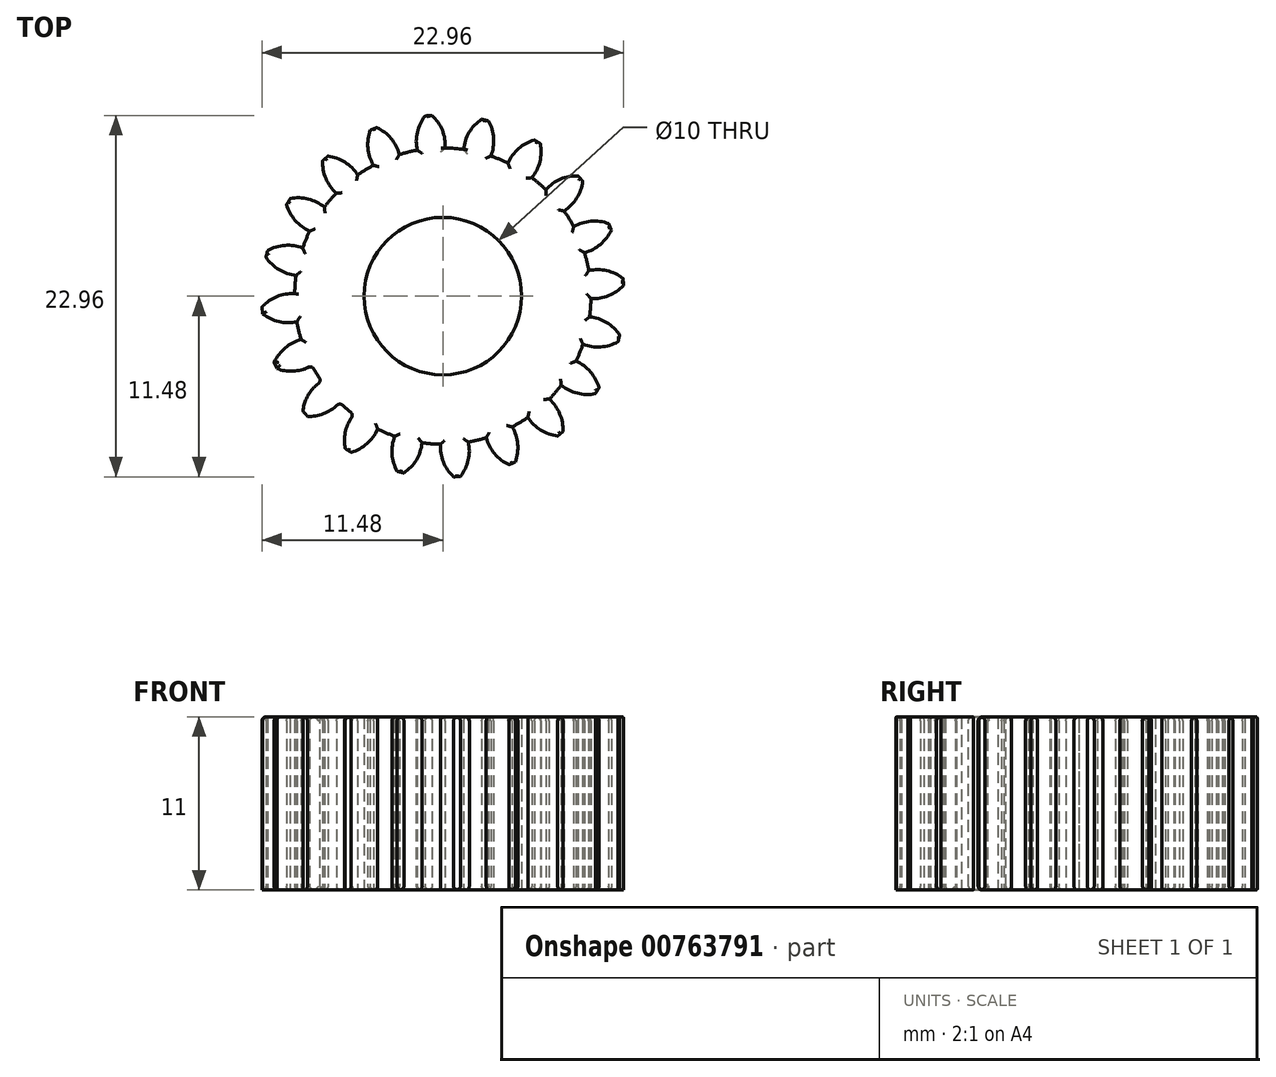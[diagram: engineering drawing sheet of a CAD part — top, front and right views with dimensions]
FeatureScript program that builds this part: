
annotation { "Feature Type Name" : "Feature", "Feature Type Description" : "" }
export const myFeature = defineFeature(function(context is Context, id is Id, definition is map)
    precondition{}
    {
        {
            assignVariable(context, id + "F0", {"name" : "GearDepth", "anyValue" : 1});
        }
        {
            assignVariable(context, id + "F1", {"name" : "TeethFillet", "anyValue" : getVariable(context, 'GearDepth') * .25});
        }
        {
            var Q0;
            Q0=qCreatedBy(makeId("Top.planeOp"),FACE);
            var sketch = newSketch(context, id + "F2", { "sketchPlane" : qUnion([Q0])});
            skCircle(sketch, "E0", {"center": v(0, 0) * mm, "radius": 9.4 * mm});
            skCircle(sketch, "E1", {"center": v(0, 0) * mm, "radius": 10.45 * mm, "construction": true});
            skCircle(sketch, "E2", {"center": v(0, 0) * mm, "radius": 11.5 * mm, "construction": true});
            skLineSegment(sketch, "E3", {"start": v(0, 0) * mm, "end": v(0, 17.6) * mm, "construction": true});
            skLineSegment(sketch, "E4", {"start": v(0, 0) * mm, "end": v(-1.42, 18) * mm, "construction": true});
            skLineSegment(sketch, "E5", {"start": v(0, 10.45) * mm, "end": v(-10.54, 10.45) * mm, "construction": true});
            skLineSegment(sketch, "E6", {"start": v(0, 10.45) * mm, "end": v(-10.3, 6.7) * mm, "construction": true});
            skCircle(sketch, "E7", {"center": v(0, 10.45) * mm, "radius": 2.61 * mm, "construction": true});
            skCircle(sketch, "E8", {"center": v(-2.46, 9.56) * mm, "radius": 2.61 * mm, "construction": true});
            skArc(sketch, "E9", {"start": v(-4.91, 10.45) * mm, "mid": v(-4.92, 10.42) * mm, "end": v(-4.94, 10.39) * mm});
            skArc(sketch, "E10.trimOffspring", {"start": v(0.15, 9.4) * mm, "mid": v(-0.03, 10.54) * mm, "end": v(-0.68, 11.48) * mm});
            skArc(sketch, "E11.MirrorCS", {"start": v(-1.62, 9.27) * mm, "mid": v(-1.62, 10.41) * mm, "end": v(-1.12, 11.45) * mm});
            skLineSegment(sketch, "E12", {"start": v(-1.12, 11.45) * mm, "end": v(-0.68, 11.48) * mm});
            skArc(sketch, "E13.1.0", {"start": v(-2.76, 9) * mm, "mid": v(-3.29, 10.01) * mm, "end": v(-4.2, 10.7) * mm});
            skLineSegment(sketch, "E13.1.1", {"start": v(-4.6, 10.54) * mm, "end": v(-4.2, 10.7) * mm});
            skArc(sketch, "E13.1.2", {"start": v(-4.4, 8.31) * mm, "mid": v(-4.76, 9.4) * mm, "end": v(-4.6, 10.54) * mm});
            skArc(sketch, "E13.2.0", {"start": v(-5.4, 7.7) * mm, "mid": v(-6.22, 8.5) * mm, "end": v(-7.3, 8.89) * mm});
            skLineSegment(sketch, "E13.2.1", {"start": v(-7.64, 8.6) * mm, "end": v(-7.3, 8.89) * mm});
            skArc(sketch, "E13.2.2", {"start": v(-6.76, 6.54) * mm, "mid": v(-7.43, 7.47) * mm, "end": v(-7.64, 8.6) * mm});
            skArc(sketch, "E13.3.0", {"start": v(-7.52, 5.65) * mm, "mid": v(-8.54, 6.17) * mm, "end": v(-9.69, 6.2) * mm});
            skLineSegment(sketch, "E13.3.1", {"start": v(-9.92, 5.82) * mm, "end": v(-9.69, 6.2) * mm});
            skArc(sketch, "E13.3.2", {"start": v(-8.45, 4.13) * mm, "mid": v(-9.37, 4.81) * mm, "end": v(-9.92, 5.82) * mm});
            skArc(sketch, "E13.4.0", {"start": v(-8.9, 3.05) * mm, "mid": v(-10.03, 3.23) * mm, "end": v(-11.13, 2.9) * mm});
            skLineSegment(sketch, "E13.4.1", {"start": v(-11.23, 2.47) * mm, "end": v(-11.13, 2.9) * mm});
            skArc(sketch, "E13.4.2", {"start": v(-9.32, 1.32) * mm, "mid": v(-10.4, 1.68) * mm, "end": v(-11.23, 2.47) * mm});
            skArc(sketch, "E13.5.0", {"start": v(-9.4, 0.15) * mm, "mid": v(-10.54, -0.03) * mm, "end": v(-11.48, -0.68) * mm});
            skLineSegment(sketch, "E13.5.1", {"start": v(-11.45, -1.12) * mm, "end": v(-11.48, -0.68) * mm});
            skArc(sketch, "E13.5.2", {"start": v(-9.27, -1.62) * mm, "mid": v(-10.41, -1.62) * mm, "end": v(-11.45, -1.12) * mm});
            skArc(sketch, "E13.6.0", {"start": v(-9, -2.76) * mm, "mid": v(-10.01, -3.29) * mm, "end": v(-10.7, -4.2) * mm});
            skLineSegment(sketch, "E13.6.1", {"start": v(-10.54, -4.6) * mm, "end": v(-10.7, -4.2) * mm});
            skArc(sketch, "E13.6.2", {"start": v(-8.31, -4.4) * mm, "mid": v(-9.4, -4.76) * mm, "end": v(-10.54, -4.6) * mm});
            skArc(sketch, "E13.7.0", {"start": v(-7.7, -5.4) * mm, "mid": v(-8.5, -6.22) * mm, "end": v(-8.89, -7.3) * mm});
            skLineSegment(sketch, "E13.7.1", {"start": v(-8.6, -7.64) * mm, "end": v(-8.89, -7.3) * mm});
            skArc(sketch, "E13.7.2", {"start": v(-6.54, -6.76) * mm, "mid": v(-7.47, -7.43) * mm, "end": v(-8.6, -7.64) * mm});
            skArc(sketch, "E13.8.0", {"start": v(-5.65, -7.52) * mm, "mid": v(-6.17, -8.54) * mm, "end": v(-6.2, -9.69) * mm});
            skLineSegment(sketch, "E13.8.1", {"start": v(-5.82, -9.92) * mm, "end": v(-6.2, -9.69) * mm});
            skArc(sketch, "E13.8.2", {"start": v(-4.13, -8.45) * mm, "mid": v(-4.81, -9.37) * mm, "end": v(-5.82, -9.92) * mm});
            skArc(sketch, "E13.9.0", {"start": v(-3.05, -8.9) * mm, "mid": v(-3.23, -10.03) * mm, "end": v(-2.9, -11.13) * mm});
            skLineSegment(sketch, "E13.9.1", {"start": v(-2.47, -11.23) * mm, "end": v(-2.9, -11.13) * mm});
            skArc(sketch, "E13.9.2", {"start": v(-1.32, -9.32) * mm, "mid": v(-1.68, -10.4) * mm, "end": v(-2.47, -11.23) * mm});
            skArc(sketch, "E13.10.0", {"start": v(-0.15, -9.4) * mm, "mid": v(0.03, -10.54) * mm, "end": v(0.68, -11.48) * mm});
            skLineSegment(sketch, "E13.10.1", {"start": v(1.12, -11.45) * mm, "end": v(0.68, -11.48) * mm});
            skArc(sketch, "E13.10.2", {"start": v(1.62, -9.27) * mm, "mid": v(1.62, -10.41) * mm, "end": v(1.12, -11.45) * mm});
            skArc(sketch, "E13.11.0", {"start": v(2.76, -9) * mm, "mid": v(3.29, -10.01) * mm, "end": v(4.2, -10.7) * mm});
            skLineSegment(sketch, "E13.11.1", {"start": v(4.6, -10.54) * mm, "end": v(4.2, -10.7) * mm});
            skArc(sketch, "E13.11.2", {"start": v(4.4, -8.31) * mm, "mid": v(4.76, -9.4) * mm, "end": v(4.6, -10.54) * mm});
            skArc(sketch, "E13.12.0", {"start": v(5.4, -7.7) * mm, "mid": v(6.22, -8.5) * mm, "end": v(7.3, -8.89) * mm});
            skLineSegment(sketch, "E13.12.1", {"start": v(7.64, -8.6) * mm, "end": v(7.3, -8.89) * mm});
            skArc(sketch, "E13.12.2", {"start": v(6.76, -6.54) * mm, "mid": v(7.43, -7.47) * mm, "end": v(7.64, -8.6) * mm});
            skArc(sketch, "E13.13.0", {"start": v(7.52, -5.65) * mm, "mid": v(8.54, -6.17) * mm, "end": v(9.69, -6.2) * mm});
            skLineSegment(sketch, "E13.13.1", {"start": v(9.92, -5.82) * mm, "end": v(9.69, -6.2) * mm});
            skArc(sketch, "E13.13.2", {"start": v(8.45, -4.13) * mm, "mid": v(9.37, -4.81) * mm, "end": v(9.92, -5.82) * mm});
            skArc(sketch, "E13.14.0", {"start": v(8.9, -3.05) * mm, "mid": v(10.03, -3.23) * mm, "end": v(11.13, -2.9) * mm});
            skLineSegment(sketch, "E13.14.1", {"start": v(11.23, -2.47) * mm, "end": v(11.13, -2.9) * mm});
            skArc(sketch, "E13.14.2", {"start": v(9.32, -1.32) * mm, "mid": v(10.4, -1.68) * mm, "end": v(11.23, -2.47) * mm});
            skArc(sketch, "E13.15.0", {"start": v(9.4, -0.15) * mm, "mid": v(10.54, 0.03) * mm, "end": v(11.48, 0.68) * mm});
            skLineSegment(sketch, "E13.15.1", {"start": v(11.45, 1.12) * mm, "end": v(11.48, 0.68) * mm});
            skArc(sketch, "E13.15.2", {"start": v(9.27, 1.62) * mm, "mid": v(10.41, 1.62) * mm, "end": v(11.45, 1.12) * mm});
            skArc(sketch, "E13.16.0", {"start": v(9, 2.76) * mm, "mid": v(10.01, 3.29) * mm, "end": v(10.7, 4.2) * mm});
            skLineSegment(sketch, "E13.16.1", {"start": v(10.54, 4.6) * mm, "end": v(10.7, 4.2) * mm});
            skArc(sketch, "E13.16.2", {"start": v(8.31, 4.4) * mm, "mid": v(9.4, 4.76) * mm, "end": v(10.54, 4.6) * mm});
            skArc(sketch, "E13.17.0", {"start": v(7.7, 5.4) * mm, "mid": v(8.5, 6.22) * mm, "end": v(8.89, 7.3) * mm});
            skLineSegment(sketch, "E13.17.1", {"start": v(8.6, 7.64) * mm, "end": v(8.89, 7.3) * mm});
            skArc(sketch, "E13.17.2", {"start": v(6.54, 6.76) * mm, "mid": v(7.47, 7.43) * mm, "end": v(8.6, 7.64) * mm});
            skArc(sketch, "E13.18.0", {"start": v(5.65, 7.52) * mm, "mid": v(6.17, 8.54) * mm, "end": v(6.2, 9.69) * mm});
            skLineSegment(sketch, "E13.18.1", {"start": v(5.82, 9.92) * mm, "end": v(6.2, 9.69) * mm});
            skArc(sketch, "E13.18.2", {"start": v(4.13, 8.45) * mm, "mid": v(4.81, 9.37) * mm, "end": v(5.82, 9.92) * mm});
            skArc(sketch, "E13.19.0", {"start": v(3.05, 8.9) * mm, "mid": v(3.23, 10.03) * mm, "end": v(2.9, 11.13) * mm});
            skLineSegment(sketch, "E13.19.1", {"start": v(2.47, 11.23) * mm, "end": v(2.9, 11.13) * mm});
            skArc(sketch, "E13.19.2", {"start": v(1.32, 9.32) * mm, "mid": v(1.68, 10.4) * mm, "end": v(2.47, 11.23) * mm});
            skCircle(sketch, "E14", {"center": v(0, 0) * mm, "radius": 5 * mm});
            skSolve(sketch);
        }
        {
            var Q0;
            {var subQ0=sQuery(id+"F2.wireOp",EDGE,"E10.trimOffspring");Q0=makeQuery(id+"F2.imprint","IMPRINT",FACE,{"disambiguationData":[TD([[makeQuery(id+"F2.imprint","IMPRINT",EDGE,{"derivedFrom":subQ0}),1.0]])]});}
            var Q1;
            {var subQ0=sQuery(id+"F2.wireOp",EDGE,"E0");var subQ1=makeQuery(id+"F2.imprint","INTERSECT",VERTEX,{"derivedFrom":[subQ0,sQuery(id+"F2.wireOp",EDGE,"E10.trimOffspring")]});Q1=makeQuery(id+"F2.imprint","IMPRINT",FACE,{"disambiguationData":[TD([[makeQuery(id+"F2.imprint","IMPRINT",EDGE,{"disambiguationData":[TD([[subQ1,-1.0]])],"derivedFrom":subQ0}),1.0]])]});}
            var Q2;
            {var subQ0=sQuery(id+"F2.wireOp",EDGE,"E13.1.0");Q2=makeQuery(id+"F2.imprint","IMPRINT",FACE,{"disambiguationData":[TD([[makeQuery(id+"F2.imprint","IMPRINT",EDGE,{"derivedFrom":subQ0}),1.0]])]});}
            var Q3;
            {var subQ0=sQuery(id+"F2.wireOp",EDGE,"E13.2.0");Q3=makeQuery(id+"F2.imprint","IMPRINT",FACE,{"disambiguationData":[TD([[makeQuery(id+"F2.imprint","IMPRINT",EDGE,{"derivedFrom":subQ0}),1.0]])]});}
            var Q4;
            {var subQ0=sQuery(id+"F2.wireOp",EDGE,"E13.3.0");Q4=makeQuery(id+"F2.imprint","IMPRINT",FACE,{"disambiguationData":[TD([[makeQuery(id+"F2.imprint","IMPRINT",EDGE,{"derivedFrom":subQ0}),1.0]])]});}
            var Q5;
            {var subQ0=sQuery(id+"F2.wireOp",EDGE,"E13.4.0");Q5=makeQuery(id+"F2.imprint","IMPRINT",FACE,{"disambiguationData":[TD([[makeQuery(id+"F2.imprint","IMPRINT",EDGE,{"derivedFrom":subQ0}),1.0]])]});}
            var Q6;
            {var subQ0=sQuery(id+"F2.wireOp",EDGE,"E13.5.0");Q6=makeQuery(id+"F2.imprint","IMPRINT",FACE,{"disambiguationData":[TD([[makeQuery(id+"F2.imprint","IMPRINT",EDGE,{"derivedFrom":subQ0}),1.0]])]});}
            var Q7;
            {var subQ0=sQuery(id+"F2.wireOp",EDGE,"E13.6.0");Q7=makeQuery(id+"F2.imprint","IMPRINT",FACE,{"disambiguationData":[TD([[makeQuery(id+"F2.imprint","IMPRINT",EDGE,{"derivedFrom":subQ0}),1.0]])]});}
            var Q8;
            {var subQ0=sQuery(id+"F2.wireOp",EDGE,"E13.7.0");Q8=makeQuery(id+"F2.imprint","IMPRINT",FACE,{"disambiguationData":[TD([[makeQuery(id+"F2.imprint","IMPRINT",EDGE,{"derivedFrom":subQ0}),1.0]])]});}
            var Q9;
            {var subQ0=sQuery(id+"F2.wireOp",EDGE,"E13.8.0");Q9=makeQuery(id+"F2.imprint","IMPRINT",FACE,{"disambiguationData":[TD([[makeQuery(id+"F2.imprint","IMPRINT",EDGE,{"derivedFrom":subQ0}),1.0]])]});}
            var Q10;
            {var subQ0=sQuery(id+"F2.wireOp",EDGE,"E13.9.0");Q10=makeQuery(id+"F2.imprint","IMPRINT",FACE,{"disambiguationData":[TD([[makeQuery(id+"F2.imprint","IMPRINT",EDGE,{"derivedFrom":subQ0}),1.0]])]});}
            var Q11;
            {var subQ0=sQuery(id+"F2.wireOp",EDGE,"E13.10.0");Q11=makeQuery(id+"F2.imprint","IMPRINT",FACE,{"disambiguationData":[TD([[makeQuery(id+"F2.imprint","IMPRINT",EDGE,{"derivedFrom":subQ0}),1.0]])]});}
            var Q12;
            {var subQ0=sQuery(id+"F2.wireOp",EDGE,"E13.11.0");Q12=makeQuery(id+"F2.imprint","IMPRINT",FACE,{"disambiguationData":[TD([[makeQuery(id+"F2.imprint","IMPRINT",EDGE,{"derivedFrom":subQ0}),1.0]])]});}
            var Q13;
            {var subQ0=sQuery(id+"F2.wireOp",EDGE,"E13.12.0");Q13=makeQuery(id+"F2.imprint","IMPRINT",FACE,{"disambiguationData":[TD([[makeQuery(id+"F2.imprint","IMPRINT",EDGE,{"derivedFrom":subQ0}),1.0]])]});}
            var Q14;
            {var subQ0=sQuery(id+"F2.wireOp",EDGE,"E13.13.0");Q14=makeQuery(id+"F2.imprint","IMPRINT",FACE,{"disambiguationData":[TD([[makeQuery(id+"F2.imprint","IMPRINT",EDGE,{"derivedFrom":subQ0}),1.0]])]});}
            var Q15;
            {var subQ0=sQuery(id+"F2.wireOp",EDGE,"E13.14.0");Q15=makeQuery(id+"F2.imprint","IMPRINT",FACE,{"disambiguationData":[TD([[makeQuery(id+"F2.imprint","IMPRINT",EDGE,{"derivedFrom":subQ0}),1.0]])]});}
            var Q16;
            {var subQ0=sQuery(id+"F2.wireOp",EDGE,"E13.15.0");Q16=makeQuery(id+"F2.imprint","IMPRINT",FACE,{"disambiguationData":[TD([[makeQuery(id+"F2.imprint","IMPRINT",EDGE,{"derivedFrom":subQ0}),1.0]])]});}
            var Q17;
            {var subQ0=sQuery(id+"F2.wireOp",EDGE,"E13.16.0");Q17=makeQuery(id+"F2.imprint","IMPRINT",FACE,{"disambiguationData":[TD([[makeQuery(id+"F2.imprint","IMPRINT",EDGE,{"derivedFrom":subQ0}),1.0]])]});}
            var Q18;
            {var subQ0=sQuery(id+"F2.wireOp",EDGE,"E13.17.0");Q18=makeQuery(id+"F2.imprint","IMPRINT",FACE,{"disambiguationData":[TD([[makeQuery(id+"F2.imprint","IMPRINT",EDGE,{"derivedFrom":subQ0}),1.0]])]});}
            var Q19;
            {var subQ0=sQuery(id+"F2.wireOp",EDGE,"E13.18.0");Q19=makeQuery(id+"F2.imprint","IMPRINT",FACE,{"disambiguationData":[TD([[makeQuery(id+"F2.imprint","IMPRINT",EDGE,{"derivedFrom":subQ0}),1.0]])]});}
            var Q20;
            {var subQ0=sQuery(id+"F2.wireOp",EDGE,"E13.19.0");Q20=makeQuery(id+"F2.imprint","IMPRINT",FACE,{"disambiguationData":[TD([[makeQuery(id+"F2.imprint","IMPRINT",EDGE,{"derivedFrom":subQ0}),1.0]])]});}
            var Q21;
            Q21=sQuery(id+"F2.wireOp",EDGE,"E0");
            var Q22;
            Q22=sQuery(id+"F2.wireOp",EDGE,"E10.trimOffspring");
            var Q23;
            Q23=sQuery(id+"F2.wireOp",EDGE,"E12");
            var Q24;
            Q24=sQuery(id+"F2.wireOp",EDGE,"E11.MirrorCS");
            extrude(context, id + "F3", {"entities" : qUnion([Q0, Q1, Q2, Q3, Q4, Q5, Q6, Q7, Q8, Q9, Q10, Q11, Q12, Q13, Q14, Q15, Q16, Q17, Q18, Q19, Q20]), "surfaceEntities" : qUnion([Q21, Q22, Q23, Q24]), "depth" : 11 * mm, "offsetDistance" : 25 * mm});
        }
        {
            var Q0;
            Q0=makeQuery(id+"F3.opExtrude","CAP_EDGE",EDGE,{"disambiguationData":[OSD([sQuery(id+"F2.wireOp",EDGE,"E13.5.2")])],"isStart":false});
            var Q1;
            Q1=makeQuery(id+"F3.opExtrude","CAP_EDGE",EDGE,{"disambiguationData":[OSD([sQuery(id+"F2.wireOp",EDGE,"E13.5.1")])],"isStart":false});
            var Q2;
            {var subQ0=sQuery(id+"F2.wireOp",EDGE,"E0");Q2=makeQuery(id+"F3.opExtrude","CAP_EDGE",EDGE,{"disambiguationData":[OSD([subQ0]),TDD([makeQuery(id+"F2.imprint","IMPRINT",EDGE,{"disambiguationData":[TD([[makeQuery(id+"F2.imprint","INTERSECT",VERTEX,{"derivedFrom":[subQ0,sQuery(id+"F2.wireOp",EDGE,"E13.5.2")]}),-1.0]])],"derivedFrom":subQ0})])],"isStart":false});}
            var Q3;
            Q3=makeQuery(id+"F3.opExtrude","CAP_EDGE",EDGE,{"disambiguationData":[OSD([sQuery(id+"F2.wireOp",EDGE,"E13.6.0")])],"isStart":false});
            var Q4;
            Q4=makeQuery(id+"F3.opExtrude","CAP_EDGE",EDGE,{"disambiguationData":[OSD([sQuery(id+"F2.wireOp",EDGE,"E13.6.1")])],"isStart":false});
            var Q5;
            Q5=makeQuery(id+"F3.opExtrude","CAP_EDGE",EDGE,{"disambiguationData":[OSD([sQuery(id+"F2.wireOp",EDGE,"E13.6.2")])],"isStart":false});
            var Q6;
            {var subQ0=sQuery(id+"F2.wireOp",EDGE,"E0");Q6=makeQuery(id+"F3.opExtrude","SWEPT_FACE",FACE,{"disambiguationData":[OSD([subQ0]),TDD([makeQuery(id+"F2.imprint","IMPRINT",EDGE,{"disambiguationData":[TD([[makeQuery(id+"F2.imprint","INTERSECT",VERTEX,{"derivedFrom":[subQ0,sQuery(id+"F2.wireOp",EDGE,"E13.6.2")]}),-1.0]])],"derivedFrom":subQ0})])]});}
            var Q7;
            {var subQ0=sQuery(id+"F2.wireOp",EDGE,"E0");Q7=makeQuery(id+"F3.opExtrude","CAP_EDGE",EDGE,{"disambiguationData":[OSD([subQ0]),TDD([makeQuery(id+"F2.imprint","IMPRINT",EDGE,{"disambiguationData":[TD([[makeQuery(id+"F2.imprint","INTERSECT",VERTEX,{"derivedFrom":[subQ0,sQuery(id+"F2.wireOp",EDGE,"E13.6.2")]}),-1.0]])],"derivedFrom":subQ0})])],"isStart":false});}
            var Q8;
            Q8=makeQuery(id+"F3.opExtrude","CAP_EDGE",EDGE,{"disambiguationData":[OSD([sQuery(id+"F2.wireOp",EDGE,"E13.7.2")])],"isStart":true});
            var Q9;
            {var subQ0=sQuery(id+"F2.wireOp",EDGE,"E0");Q9=makeQuery(id+"F3.opExtrude","CAP_EDGE",EDGE,{"disambiguationData":[OSD([subQ0]),TDD([makeQuery(id+"F2.imprint","IMPRINT",EDGE,{"disambiguationData":[TD([[makeQuery(id+"F2.imprint","INTERSECT",VERTEX,{"derivedFrom":[subQ0,sQuery(id+"F2.wireOp",EDGE,"E13.7.2")]}),-1.0]])],"derivedFrom":subQ0})])],"isStart":true});}
            var Q10;
            Q10=makeQuery(id+"F3.opExtrude","CAP_EDGE",EDGE,{"disambiguationData":[OSD([sQuery(id+"F2.wireOp",EDGE,"E13.7.2")])],"isStart":false});
            var Q11;
            {var subQ0=sQuery(id+"F2.wireOp",EDGE,"E0");Q11=makeQuery(id+"F3.opExtrude","CAP_EDGE",EDGE,{"disambiguationData":[OSD([subQ0]),TDD([makeQuery(id+"F2.imprint","IMPRINT",EDGE,{"disambiguationData":[TD([[makeQuery(id+"F2.imprint","INTERSECT",VERTEX,{"derivedFrom":[subQ0,sQuery(id+"F2.wireOp",EDGE,"E13.7.2")]}),-1.0]])],"derivedFrom":subQ0})])],"isStart":false});}
            var Q12;
            Q12=makeQuery(id+"F3.opExtrude","CAP_EDGE",EDGE,{"disambiguationData":[OSD([sQuery(id+"F2.wireOp",EDGE,"E13.8.0")])],"isStart":false});
            var Q13;
            {var subQ0=sQuery(id+"F2.wireOp",EDGE,"E0");Q13=makeQuery(id+"F3.opExtrude","SWEPT_FACE",FACE,{"disambiguationData":[OSD([subQ0]),TDD([makeQuery(id+"F2.imprint","IMPRINT",EDGE,{"disambiguationData":[TD([[makeQuery(id+"F2.imprint","INTERSECT",VERTEX,{"derivedFrom":[subQ0,sQuery(id+"F2.wireOp",EDGE,"E13.7.2")]}),-1.0]])],"derivedFrom":subQ0})])]});}
            var Q14;
            Q14=makeQuery(id+"F3.opExtrude","CAP_EDGE",EDGE,{"disambiguationData":[OSD([sQuery(id+"F2.wireOp",EDGE,"E13.6.0")])],"isStart":true});
            var Q15;
            Q15=makeQuery(id+"F3.opExtrude","CAP_EDGE",EDGE,{"disambiguationData":[OSD([sQuery(id+"F2.wireOp",EDGE,"E13.8.2")])],"isStart":false});
            var Q16;
            {var subQ0=sQuery(id+"F2.wireOp",EDGE,"E0");Q16=makeQuery(id+"F3.opExtrude","CAP_EDGE",EDGE,{"disambiguationData":[OSD([subQ0]),TDD([makeQuery(id+"F2.imprint","IMPRINT",EDGE,{"disambiguationData":[TD([[makeQuery(id+"F2.imprint","INTERSECT",VERTEX,{"derivedFrom":[subQ0,sQuery(id+"F2.wireOp",EDGE,"E13.8.2")]}),-1.0]])],"derivedFrom":subQ0})])],"isStart":false});}
            var Q17;
            Q17=makeQuery(id+"F3.opExtrude","CAP_EDGE",EDGE,{"disambiguationData":[OSD([sQuery(id+"F2.wireOp",EDGE,"E13.9.0")])],"isStart":false});
            var Q18;
            Q18=makeQuery(id+"F3.opExtrude","CAP_EDGE",EDGE,{"disambiguationData":[OSD([sQuery(id+"F2.wireOp",EDGE,"E13.9.2")])],"isStart":false});
            var Q19;
            {var subQ0=sQuery(id+"F2.wireOp",EDGE,"E0");Q19=makeQuery(id+"F3.opExtrude","CAP_EDGE",EDGE,{"disambiguationData":[OSD([subQ0]),TDD([makeQuery(id+"F2.imprint","IMPRINT",EDGE,{"disambiguationData":[TD([[makeQuery(id+"F2.imprint","INTERSECT",VERTEX,{"derivedFrom":[subQ0,sQuery(id+"F2.wireOp",EDGE,"E13.9.2")]}),-1.0]])],"derivedFrom":subQ0})])],"isStart":false});}
            var Q20;
            Q20=makeQuery(id+"F3.opExtrude","CAP_EDGE",EDGE,{"disambiguationData":[OSD([sQuery(id+"F2.wireOp",EDGE,"E13.10.0")])],"isStart":false});
            var Q21;
            Q21=makeQuery(id+"F3.opExtrude","CAP_EDGE",EDGE,{"disambiguationData":[OSD([sQuery(id+"F2.wireOp",EDGE,"E13.10.2")])],"isStart":false});
            var Q22;
            {var subQ0=sQuery(id+"F2.wireOp",EDGE,"E0");Q22=makeQuery(id+"F3.opExtrude","CAP_EDGE",EDGE,{"disambiguationData":[OSD([subQ0]),TDD([makeQuery(id+"F2.imprint","IMPRINT",EDGE,{"disambiguationData":[TD([[makeQuery(id+"F2.imprint","INTERSECT",VERTEX,{"derivedFrom":[subQ0,sQuery(id+"F2.wireOp",EDGE,"E13.10.2")]}),-1.0]])],"derivedFrom":subQ0})])],"isStart":false});}
            var Q23;
            Q23=makeQuery(id+"F3.opExtrude","CAP_EDGE",EDGE,{"disambiguationData":[OSD([sQuery(id+"F2.wireOp",EDGE,"E13.11.0")])],"isStart":false});
            var Q24;
            Q24=makeQuery(id+"F3.opExtrude","CAP_EDGE",EDGE,{"disambiguationData":[OSD([sQuery(id+"F2.wireOp",EDGE,"E13.11.2")])],"isStart":false});
            var Q25;
            {var subQ0=sQuery(id+"F2.wireOp",EDGE,"E0");Q25=makeQuery(id+"F3.opExtrude","CAP_EDGE",EDGE,{"disambiguationData":[OSD([subQ0]),TDD([makeQuery(id+"F2.imprint","IMPRINT",EDGE,{"disambiguationData":[TD([[makeQuery(id+"F2.imprint","INTERSECT",VERTEX,{"derivedFrom":[subQ0,sQuery(id+"F2.wireOp",EDGE,"E13.11.2")]}),-1.0]])],"derivedFrom":subQ0})])],"isStart":false});}
            var Q26;
            Q26=makeQuery(id+"F3.opExtrude","CAP_EDGE",EDGE,{"disambiguationData":[OSD([sQuery(id+"F2.wireOp",EDGE,"E13.12.0")])],"isStart":false});
            var Q27;
            Q27=makeQuery(id+"F3.opExtrude","CAP_EDGE",EDGE,{"disambiguationData":[OSD([sQuery(id+"F2.wireOp",EDGE,"E13.12.2")])],"isStart":false});
            var Q28;
            {var subQ0=sQuery(id+"F2.wireOp",EDGE,"E0");Q28=makeQuery(id+"F3.opExtrude","CAP_EDGE",EDGE,{"disambiguationData":[OSD([subQ0]),TDD([makeQuery(id+"F2.imprint","IMPRINT",EDGE,{"disambiguationData":[TD([[makeQuery(id+"F2.imprint","INTERSECT",VERTEX,{"derivedFrom":[subQ0,sQuery(id+"F2.wireOp",EDGE,"E13.12.2")]}),-1.0]])],"derivedFrom":subQ0})])],"isStart":false});}
            var Q29;
            Q29=makeQuery(id+"F3.opExtrude","CAP_EDGE",EDGE,{"disambiguationData":[OSD([sQuery(id+"F2.wireOp",EDGE,"E13.13.0")])],"isStart":false});
            var Q30;
            Q30=makeQuery(id+"F3.opExtrude","CAP_EDGE",EDGE,{"disambiguationData":[OSD([sQuery(id+"F2.wireOp",EDGE,"E13.13.2")])],"isStart":false});
            var Q31;
            {var subQ0=sQuery(id+"F2.wireOp",EDGE,"E0");Q31=makeQuery(id+"F3.opExtrude","CAP_EDGE",EDGE,{"disambiguationData":[OSD([subQ0]),TDD([makeQuery(id+"F2.imprint","IMPRINT",EDGE,{"disambiguationData":[TD([[makeQuery(id+"F2.imprint","INTERSECT",VERTEX,{"derivedFrom":[subQ0,sQuery(id+"F2.wireOp",EDGE,"E13.13.2")]}),-1.0]])],"derivedFrom":subQ0})])],"isStart":false});}
            var Q32;
            Q32=makeQuery(id+"F3.opExtrude","CAP_EDGE",EDGE,{"disambiguationData":[OSD([sQuery(id+"F2.wireOp",EDGE,"E13.14.0")])],"isStart":false});
            var Q33;
            Q33=makeQuery(id+"F3.opExtrude","CAP_EDGE",EDGE,{"disambiguationData":[OSD([sQuery(id+"F2.wireOp",EDGE,"E13.14.2")])],"isStart":false});
            var Q34;
            {var subQ0=sQuery(id+"F2.wireOp",EDGE,"E0");Q34=makeQuery(id+"F3.opExtrude","CAP_EDGE",EDGE,{"disambiguationData":[OSD([subQ0]),TDD([makeQuery(id+"F2.imprint","IMPRINT",EDGE,{"disambiguationData":[TD([[makeQuery(id+"F2.imprint","INTERSECT",VERTEX,{"derivedFrom":[subQ0,sQuery(id+"F2.wireOp",EDGE,"E13.14.2")]}),-1.0]])],"derivedFrom":subQ0})])],"isStart":false});}
            var Q35;
            Q35=makeQuery(id+"F3.opExtrude","CAP_EDGE",EDGE,{"disambiguationData":[OSD([sQuery(id+"F2.wireOp",EDGE,"E13.15.0")])],"isStart":false});
            var Q36;
            {var subQ0=sQuery(id+"F2.wireOp",EDGE,"E0");Q36=makeQuery(id+"F3.opExtrude","CAP_EDGE",EDGE,{"disambiguationData":[OSD([subQ0]),TDD([makeQuery(id+"F2.imprint","IMPRINT",EDGE,{"disambiguationData":[TD([[makeQuery(id+"F2.imprint","INTERSECT",VERTEX,{"derivedFrom":[subQ0,sQuery(id+"F2.wireOp",EDGE,"E13.14.2")]}),-1.0]])],"derivedFrom":subQ0})])],"isStart":false});}
            var Q37;
            Q37=makeQuery(id+"F3.opExtrude","CAP_EDGE",EDGE,{"disambiguationData":[OSD([sQuery(id+"F2.wireOp",EDGE,"E13.15.2")])],"isStart":false});
            var Q38;
            {var subQ0=sQuery(id+"F2.wireOp",EDGE,"E0");Q38=makeQuery(id+"F3.opExtrude","CAP_EDGE",EDGE,{"disambiguationData":[OSD([subQ0]),TDD([makeQuery(id+"F2.imprint","IMPRINT",EDGE,{"disambiguationData":[TD([[makeQuery(id+"F2.imprint","INTERSECT",VERTEX,{"derivedFrom":[subQ0,sQuery(id+"F2.wireOp",EDGE,"E13.15.2")]}),-1.0]])],"derivedFrom":subQ0})])],"isStart":false});}
            var Q39;
            Q39=makeQuery(id+"F3.opExtrude","CAP_EDGE",EDGE,{"disambiguationData":[OSD([sQuery(id+"F2.wireOp",EDGE,"E13.16.0")])],"isStart":false});
            var Q40;
            Q40=makeQuery(id+"F3.opExtrude","CAP_EDGE",EDGE,{"disambiguationData":[OSD([sQuery(id+"F2.wireOp",EDGE,"E13.16.2")])],"isStart":false});
            var Q41;
            Q41=makeQuery(id+"F3.opExtrude","CAP_EDGE",EDGE,{"disambiguationData":[OSD([sQuery(id+"F2.wireOp",EDGE,"E13.17.0")])],"isStart":false});
            var Q42;
            {var subQ0=sQuery(id+"F2.wireOp",EDGE,"E0");Q42=makeQuery(id+"F3.opExtrude","CAP_EDGE",EDGE,{"disambiguationData":[OSD([subQ0]),TDD([makeQuery(id+"F2.imprint","IMPRINT",EDGE,{"disambiguationData":[TD([[makeQuery(id+"F2.imprint","INTERSECT",VERTEX,{"derivedFrom":[subQ0,sQuery(id+"F2.wireOp",EDGE,"E13.16.2")]}),-1.0]])],"derivedFrom":subQ0})])],"isStart":false});}
            var Q43;
            Q43=makeQuery(id+"F3.opExtrude","CAP_EDGE",EDGE,{"disambiguationData":[OSD([sQuery(id+"F2.wireOp",EDGE,"E13.17.2")])],"isStart":false});
            var Q44;
            {var subQ0=sQuery(id+"F2.wireOp",EDGE,"E0");Q44=makeQuery(id+"F3.opExtrude","CAP_EDGE",EDGE,{"disambiguationData":[OSD([subQ0]),TDD([makeQuery(id+"F2.imprint","IMPRINT",EDGE,{"disambiguationData":[TD([[makeQuery(id+"F2.imprint","INTERSECT",VERTEX,{"derivedFrom":[subQ0,sQuery(id+"F2.wireOp",EDGE,"E13.17.2")]}),-1.0]])],"derivedFrom":subQ0})])],"isStart":false});}
            var Q45;
            Q45=makeQuery(id+"F3.opExtrude","CAP_EDGE",EDGE,{"disambiguationData":[OSD([sQuery(id+"F2.wireOp",EDGE,"E13.18.0")])],"isStart":false});
            var Q46;
            Q46=makeQuery(id+"F3.opExtrude","CAP_EDGE",EDGE,{"disambiguationData":[OSD([sQuery(id+"F2.wireOp",EDGE,"E13.18.2")])],"isStart":false});
            var Q47;
            {var subQ0=sQuery(id+"F2.wireOp",EDGE,"E0");Q47=makeQuery(id+"F3.opExtrude","CAP_EDGE",EDGE,{"disambiguationData":[OSD([subQ0]),TDD([makeQuery(id+"F2.imprint","IMPRINT",EDGE,{"disambiguationData":[TD([[makeQuery(id+"F2.imprint","INTERSECT",VERTEX,{"derivedFrom":[subQ0,sQuery(id+"F2.wireOp",EDGE,"E13.18.2")]}),-1.0]])],"derivedFrom":subQ0})])],"isStart":false});}
            var Q48;
            Q48=makeQuery(id+"F3.opExtrude","CAP_EDGE",EDGE,{"disambiguationData":[OSD([sQuery(id+"F2.wireOp",EDGE,"E13.19.0")])],"isStart":false});
            var Q49;
            Q49=makeQuery(id+"F3.opExtrude","CAP_EDGE",EDGE,{"disambiguationData":[OSD([sQuery(id+"F2.wireOp",EDGE,"E13.19.2")])],"isStart":false});
            var Q50;
            Q50=makeQuery(id+"F3.opExtrude","CAP_EDGE",EDGE,{"disambiguationData":[OSD([sQuery(id+"F2.wireOp",EDGE,"E10.trimOffspring")])],"isStart":false});
            var Q51;
            Q51=makeQuery(id+"F3.opExtrude","CAP_EDGE",EDGE,{"disambiguationData":[OSD([sQuery(id+"F2.wireOp",EDGE,"E11.MirrorCS")])],"isStart":false});
            var Q52;
            {var subQ0=sQuery(id+"F2.wireOp",EDGE,"E0");Q52=makeQuery(id+"F3.opExtrude","CAP_EDGE",EDGE,{"disambiguationData":[OSD([subQ0]),TDD([makeQuery(id+"F2.imprint","IMPRINT",EDGE,{"disambiguationData":[TD([[makeQuery(id+"F2.imprint","INTERSECT",VERTEX,{"derivedFrom":[subQ0,sQuery(id+"F2.wireOp",EDGE,"E11.MirrorCS")]}),-1.0]])],"derivedFrom":subQ0})])],"isStart":false});}
            var Q53;
            Q53=makeQuery(id+"F3.opExtrude","CAP_EDGE",EDGE,{"disambiguationData":[OSD([sQuery(id+"F2.wireOp",EDGE,"E13.1.0")])],"isStart":false});
            var Q54;
            Q54=makeQuery(id+"F3.opExtrude","CAP_EDGE",EDGE,{"disambiguationData":[OSD([sQuery(id+"F2.wireOp",EDGE,"E13.1.2")])],"isStart":false});
            var Q55;
            {var subQ0=sQuery(id+"F2.wireOp",EDGE,"E0");Q55=makeQuery(id+"F3.opExtrude","CAP_EDGE",EDGE,{"disambiguationData":[OSD([subQ0]),TDD([makeQuery(id+"F2.imprint","IMPRINT",EDGE,{"disambiguationData":[TD([[makeQuery(id+"F2.imprint","INTERSECT",VERTEX,{"derivedFrom":[subQ0,sQuery(id+"F2.wireOp",EDGE,"E13.1.2")]}),-1.0]])],"derivedFrom":subQ0})])],"isStart":false});}
            var Q56;
            Q56=makeQuery(id+"F3.opExtrude","CAP_EDGE",EDGE,{"disambiguationData":[OSD([sQuery(id+"F2.wireOp",EDGE,"E13.2.0")])],"isStart":false});
            var Q57;
            Q57=makeQuery(id+"F3.opExtrude","CAP_EDGE",EDGE,{"disambiguationData":[OSD([sQuery(id+"F2.wireOp",EDGE,"E13.2.2")])],"isStart":false});
            var Q58;
            {var subQ0=sQuery(id+"F2.wireOp",EDGE,"E0");Q58=makeQuery(id+"F3.opExtrude","CAP_EDGE",EDGE,{"disambiguationData":[OSD([subQ0]),TDD([makeQuery(id+"F2.imprint","IMPRINT",EDGE,{"disambiguationData":[TD([[makeQuery(id+"F2.imprint","INTERSECT",VERTEX,{"derivedFrom":[subQ0,sQuery(id+"F2.wireOp",EDGE,"E13.2.2")]}),-1.0]])],"derivedFrom":subQ0})])],"isStart":false});}
            var Q59;
            Q59=makeQuery(id+"F3.opExtrude","CAP_EDGE",EDGE,{"disambiguationData":[OSD([sQuery(id+"F2.wireOp",EDGE,"E13.3.0")])],"isStart":false});
            var Q60;
            Q60=makeQuery(id+"F3.opExtrude","CAP_EDGE",EDGE,{"disambiguationData":[OSD([sQuery(id+"F2.wireOp",EDGE,"E13.3.2")])],"isStart":false});
            var Q61;
            {var subQ0=sQuery(id+"F2.wireOp",EDGE,"E0");Q61=makeQuery(id+"F3.opExtrude","CAP_EDGE",EDGE,{"disambiguationData":[OSD([subQ0]),TDD([makeQuery(id+"F2.imprint","IMPRINT",EDGE,{"disambiguationData":[TD([[makeQuery(id+"F2.imprint","INTERSECT",VERTEX,{"derivedFrom":[subQ0,sQuery(id+"F2.wireOp",EDGE,"E13.3.2")]}),-1.0]])],"derivedFrom":subQ0})])],"isStart":false});}
            var Q62;
            Q62=makeQuery(id+"F3.opExtrude","CAP_EDGE",EDGE,{"disambiguationData":[OSD([sQuery(id+"F2.wireOp",EDGE,"E13.4.0")])],"isStart":false});
            var Q63;
            Q63=makeQuery(id+"F3.opExtrude","CAP_EDGE",EDGE,{"disambiguationData":[OSD([sQuery(id+"F2.wireOp",EDGE,"E13.4.2")])],"isStart":false});
            var Q64;
            {var subQ0=sQuery(id+"F2.wireOp",EDGE,"E0");Q64=makeQuery(id+"F3.opExtrude","CAP_EDGE",EDGE,{"disambiguationData":[OSD([subQ0]),TDD([makeQuery(id+"F2.imprint","IMPRINT",EDGE,{"disambiguationData":[TD([[makeQuery(id+"F2.imprint","INTERSECT",VERTEX,{"derivedFrom":[subQ0,sQuery(id+"F2.wireOp",EDGE,"E13.4.2")]}),-1.0]])],"derivedFrom":subQ0})])],"isStart":false});}
            var Q65;
            {var subQ0=sQuery(id+"F2.wireOp",EDGE,"E0");Q65=makeQuery(id+"F3.opExtrude","CAP_EDGE",EDGE,{"disambiguationData":[OSD([subQ0]),TDD([makeQuery(id+"F2.imprint","IMPRINT",EDGE,{"disambiguationData":[TD([[makeQuery(id+"F2.imprint","INTERSECT",VERTEX,{"derivedFrom":[subQ0,sQuery(id+"F2.wireOp",EDGE,"E13.5.2")]}),-1.0]])],"derivedFrom":subQ0})])],"isStart":true});}
            var Q66;
            Q66=makeQuery(id+"F3.opExtrude","CAP_EDGE",EDGE,{"disambiguationData":[OSD([sQuery(id+"F2.wireOp",EDGE,"E13.5.2")])],"isStart":true});
            var Q67;
            {var subQ0=sQuery(id+"F2.wireOp",EDGE,"E0");Q67=makeQuery(id+"F3.opExtrude","CAP_EDGE",EDGE,{"disambiguationData":[OSD([subQ0]),TDD([makeQuery(id+"F2.imprint","IMPRINT",EDGE,{"disambiguationData":[TD([[makeQuery(id+"F2.imprint","INTERSECT",VERTEX,{"derivedFrom":[subQ0,sQuery(id+"F2.wireOp",EDGE,"E13.4.2")]}),-1.0]])],"derivedFrom":subQ0})])],"isStart":true});}
            var Q68;
            Q68=makeQuery(id+"F3.opExtrude","CAP_EDGE",EDGE,{"disambiguationData":[OSD([sQuery(id+"F2.wireOp",EDGE,"E13.4.2")])],"isStart":true});
            var Q69;
            Q69=makeQuery(id+"F3.opExtrude","CAP_EDGE",EDGE,{"disambiguationData":[OSD([sQuery(id+"F2.wireOp",EDGE,"E13.4.0")])],"isStart":true});
            var Q70;
            {var subQ0=sQuery(id+"F2.wireOp",EDGE,"E0");Q70=makeQuery(id+"F3.opExtrude","CAP_EDGE",EDGE,{"disambiguationData":[OSD([subQ0]),TDD([makeQuery(id+"F2.imprint","IMPRINT",EDGE,{"disambiguationData":[TD([[makeQuery(id+"F2.imprint","INTERSECT",VERTEX,{"derivedFrom":[subQ0,sQuery(id+"F2.wireOp",EDGE,"E13.3.2")]}),-1.0]])],"derivedFrom":subQ0})])],"isStart":true});}
            var Q71;
            Q71=makeQuery(id+"F3.opExtrude","CAP_EDGE",EDGE,{"disambiguationData":[OSD([sQuery(id+"F2.wireOp",EDGE,"E13.3.2")])],"isStart":true});
            var Q72;
            Q72=makeQuery(id+"F3.opExtrude","CAP_EDGE",EDGE,{"disambiguationData":[OSD([sQuery(id+"F2.wireOp",EDGE,"E13.3.0")])],"isStart":true});
            var Q73;
            {var subQ0=sQuery(id+"F2.wireOp",EDGE,"E0");Q73=makeQuery(id+"F3.opExtrude","CAP_EDGE",EDGE,{"disambiguationData":[OSD([subQ0]),TDD([makeQuery(id+"F2.imprint","IMPRINT",EDGE,{"disambiguationData":[TD([[makeQuery(id+"F2.imprint","INTERSECT",VERTEX,{"derivedFrom":[subQ0,sQuery(id+"F2.wireOp",EDGE,"E13.2.2")]}),-1.0]])],"derivedFrom":subQ0})])],"isStart":true});}
            var Q74;
            Q74=makeQuery(id+"F3.opExtrude","CAP_EDGE",EDGE,{"disambiguationData":[OSD([sQuery(id+"F2.wireOp",EDGE,"E13.2.2")])],"isStart":true});
            var Q75;
            Q75=makeQuery(id+"F3.opExtrude","CAP_EDGE",EDGE,{"disambiguationData":[OSD([sQuery(id+"F2.wireOp",EDGE,"E13.2.0")])],"isStart":true});
            var Q76;
            Q76=makeQuery(id+"F3.opExtrude","CAP_EDGE",EDGE,{"disambiguationData":[OSD([sQuery(id+"F2.wireOp",EDGE,"E13.1.2")])],"isStart":true});
            var Q77;
            {var subQ0=sQuery(id+"F2.wireOp",EDGE,"E0");Q77=makeQuery(id+"F3.opExtrude","CAP_EDGE",EDGE,{"disambiguationData":[OSD([subQ0]),TDD([makeQuery(id+"F2.imprint","IMPRINT",EDGE,{"disambiguationData":[TD([[makeQuery(id+"F2.imprint","INTERSECT",VERTEX,{"derivedFrom":[subQ0,sQuery(id+"F2.wireOp",EDGE,"E13.1.2")]}),-1.0]])],"derivedFrom":subQ0})])],"isStart":true});}
            var Q78;
            Q78=makeQuery(id+"F3.opExtrude","CAP_EDGE",EDGE,{"disambiguationData":[OSD([sQuery(id+"F2.wireOp",EDGE,"E13.1.0")])],"isStart":true});
            var Q79;
            {var subQ0=sQuery(id+"F2.wireOp",EDGE,"E0");Q79=makeQuery(id+"F3.opExtrude","CAP_EDGE",EDGE,{"disambiguationData":[OSD([subQ0]),TDD([makeQuery(id+"F2.imprint","IMPRINT",EDGE,{"disambiguationData":[TD([[makeQuery(id+"F2.imprint","INTERSECT",VERTEX,{"derivedFrom":[subQ0,sQuery(id+"F2.wireOp",EDGE,"E11.MirrorCS")]}),-1.0]])],"derivedFrom":subQ0})])],"isStart":true});}
            var Q80;
            Q80=makeQuery(id+"F3.opExtrude","CAP_EDGE",EDGE,{"disambiguationData":[OSD([sQuery(id+"F2.wireOp",EDGE,"E11.MirrorCS")])],"isStart":true});
            var Q81;
            Q81=makeQuery(id+"F3.opExtrude","CAP_EDGE",EDGE,{"disambiguationData":[OSD([sQuery(id+"F2.wireOp",EDGE,"E10.trimOffspring")])],"isStart":true});
            var Q82;
            {var subQ0=sQuery(id+"F2.wireOp",EDGE,"E0");Q82=makeQuery(id+"F3.opExtrude","CAP_EDGE",EDGE,{"disambiguationData":[OSD([subQ0]),TDD([makeQuery(id+"F2.imprint","IMPRINT",EDGE,{"disambiguationData":[TD([[makeQuery(id+"F2.imprint","INTERSECT",VERTEX,{"derivedFrom":[subQ0,sQuery(id+"F2.wireOp",EDGE,"E10.trimOffspring")]}),1.0]])],"derivedFrom":subQ0})])],"isStart":true});}
            var Q83;
            Q83=makeQuery(id+"F3.opExtrude","CAP_EDGE",EDGE,{"disambiguationData":[OSD([sQuery(id+"F2.wireOp",EDGE,"E13.19.2")])],"isStart":true});
            var Q84;
            Q84=makeQuery(id+"F3.opExtrude","CAP_EDGE",EDGE,{"disambiguationData":[OSD([sQuery(id+"F2.wireOp",EDGE,"E13.19.0")])],"isStart":true});
            var Q85;
            {var subQ0=sQuery(id+"F2.wireOp",EDGE,"E0");Q85=makeQuery(id+"F3.opExtrude","CAP_EDGE",EDGE,{"disambiguationData":[OSD([subQ0]),TDD([makeQuery(id+"F2.imprint","IMPRINT",EDGE,{"disambiguationData":[TD([[makeQuery(id+"F2.imprint","INTERSECT",VERTEX,{"derivedFrom":[subQ0,sQuery(id+"F2.wireOp",EDGE,"E13.18.2")]}),-1.0]])],"derivedFrom":subQ0})])],"isStart":true});}
            var Q86;
            Q86=makeQuery(id+"F3.opExtrude","CAP_EDGE",EDGE,{"disambiguationData":[OSD([sQuery(id+"F2.wireOp",EDGE,"E13.18.2")])],"isStart":true});
            var Q87;
            Q87=makeQuery(id+"F3.opExtrude","CAP_EDGE",EDGE,{"disambiguationData":[OSD([sQuery(id+"F2.wireOp",EDGE,"E13.18.0")])],"isStart":true});
            var Q88;
            {var subQ0=sQuery(id+"F2.wireOp",EDGE,"E0");Q88=makeQuery(id+"F3.opExtrude","CAP_EDGE",EDGE,{"disambiguationData":[OSD([subQ0]),TDD([makeQuery(id+"F2.imprint","IMPRINT",EDGE,{"disambiguationData":[TD([[makeQuery(id+"F2.imprint","INTERSECT",VERTEX,{"derivedFrom":[subQ0,sQuery(id+"F2.wireOp",EDGE,"E13.17.2")]}),-1.0]])],"derivedFrom":subQ0})])],"isStart":true});}
            var Q89;
            Q89=makeQuery(id+"F3.opExtrude","CAP_EDGE",EDGE,{"disambiguationData":[OSD([sQuery(id+"F2.wireOp",EDGE,"E13.17.2")])],"isStart":true});
            var Q90;
            Q90=makeQuery(id+"F3.opExtrude","CAP_EDGE",EDGE,{"disambiguationData":[OSD([sQuery(id+"F2.wireOp",EDGE,"E13.17.0")])],"isStart":true});
            var Q91;
            {var subQ0=sQuery(id+"F2.wireOp",EDGE,"E0");Q91=makeQuery(id+"F3.opExtrude","CAP_EDGE",EDGE,{"disambiguationData":[OSD([subQ0]),TDD([makeQuery(id+"F2.imprint","IMPRINT",EDGE,{"disambiguationData":[TD([[makeQuery(id+"F2.imprint","INTERSECT",VERTEX,{"derivedFrom":[subQ0,sQuery(id+"F2.wireOp",EDGE,"E13.16.2")]}),-1.0]])],"derivedFrom":subQ0})])],"isStart":true});}
            var Q92;
            Q92=makeQuery(id+"F3.opExtrude","CAP_EDGE",EDGE,{"disambiguationData":[OSD([sQuery(id+"F2.wireOp",EDGE,"E13.16.2")])],"isStart":true});
            var Q93;
            Q93=makeQuery(id+"F3.opExtrude","CAP_EDGE",EDGE,{"disambiguationData":[OSD([sQuery(id+"F2.wireOp",EDGE,"E13.16.0")])],"isStart":true});
            var Q94;
            {var subQ0=sQuery(id+"F2.wireOp",EDGE,"E0");Q94=makeQuery(id+"F3.opExtrude","CAP_EDGE",EDGE,{"disambiguationData":[OSD([subQ0]),TDD([makeQuery(id+"F2.imprint","IMPRINT",EDGE,{"disambiguationData":[TD([[makeQuery(id+"F2.imprint","INTERSECT",VERTEX,{"derivedFrom":[subQ0,sQuery(id+"F2.wireOp",EDGE,"E13.15.2")]}),-1.0]])],"derivedFrom":subQ0})])],"isStart":true});}
            var Q95;
            Q95=makeQuery(id+"F3.opExtrude","CAP_EDGE",EDGE,{"disambiguationData":[OSD([sQuery(id+"F2.wireOp",EDGE,"E13.15.2")])],"isStart":true});
            var Q96;
            Q96=makeQuery(id+"F3.opExtrude","CAP_EDGE",EDGE,{"disambiguationData":[OSD([sQuery(id+"F2.wireOp",EDGE,"E13.15.0")])],"isStart":true});
            var Q97;
            {var subQ0=sQuery(id+"F2.wireOp",EDGE,"E0");Q97=makeQuery(id+"F3.opExtrude","CAP_EDGE",EDGE,{"disambiguationData":[OSD([subQ0]),TDD([makeQuery(id+"F2.imprint","IMPRINT",EDGE,{"disambiguationData":[TD([[makeQuery(id+"F2.imprint","INTERSECT",VERTEX,{"derivedFrom":[subQ0,sQuery(id+"F2.wireOp",EDGE,"E13.14.2")]}),-1.0]])],"derivedFrom":subQ0})])],"isStart":true});}
            var Q98;
            Q98=makeQuery(id+"F3.opExtrude","CAP_EDGE",EDGE,{"disambiguationData":[OSD([sQuery(id+"F2.wireOp",EDGE,"E13.14.2")])],"isStart":true});
            var Q99;
            Q99=makeQuery(id+"F3.opExtrude","CAP_EDGE",EDGE,{"disambiguationData":[OSD([sQuery(id+"F2.wireOp",EDGE,"E13.14.0")])],"isStart":true});
            var Q100;
            {var subQ0=sQuery(id+"F2.wireOp",EDGE,"E0");Q100=makeQuery(id+"F3.opExtrude","CAP_EDGE",EDGE,{"disambiguationData":[OSD([subQ0]),TDD([makeQuery(id+"F2.imprint","IMPRINT",EDGE,{"disambiguationData":[TD([[makeQuery(id+"F2.imprint","INTERSECT",VERTEX,{"derivedFrom":[subQ0,sQuery(id+"F2.wireOp",EDGE,"E13.13.2")]}),-1.0]])],"derivedFrom":subQ0})])],"isStart":true});}
            var Q101;
            Q101=makeQuery(id+"F3.opExtrude","CAP_EDGE",EDGE,{"disambiguationData":[OSD([sQuery(id+"F2.wireOp",EDGE,"E13.13.2")])],"isStart":true});
            var Q102;
            Q102=makeQuery(id+"F3.opExtrude","CAP_EDGE",EDGE,{"disambiguationData":[OSD([sQuery(id+"F2.wireOp",EDGE,"E13.13.0")])],"isStart":true});
            var Q103;
            {var subQ0=sQuery(id+"F2.wireOp",EDGE,"E0");Q103=makeQuery(id+"F3.opExtrude","CAP_EDGE",EDGE,{"disambiguationData":[OSD([subQ0]),TDD([makeQuery(id+"F2.imprint","IMPRINT",EDGE,{"disambiguationData":[TD([[makeQuery(id+"F2.imprint","INTERSECT",VERTEX,{"derivedFrom":[subQ0,sQuery(id+"F2.wireOp",EDGE,"E13.12.2")]}),-1.0]])],"derivedFrom":subQ0})])],"isStart":true});}
            var Q104;
            Q104=makeQuery(id+"F3.opExtrude","CAP_EDGE",EDGE,{"disambiguationData":[OSD([sQuery(id+"F2.wireOp",EDGE,"E13.12.2")])],"isStart":true});
            var Q105;
            Q105=makeQuery(id+"F3.opExtrude","CAP_EDGE",EDGE,{"disambiguationData":[OSD([sQuery(id+"F2.wireOp",EDGE,"E13.12.0")])],"isStart":true});
            var Q106;
            {var subQ0=sQuery(id+"F2.wireOp",EDGE,"E0");Q106=makeQuery(id+"F3.opExtrude","CAP_EDGE",EDGE,{"disambiguationData":[OSD([subQ0]),TDD([makeQuery(id+"F2.imprint","IMPRINT",EDGE,{"disambiguationData":[TD([[makeQuery(id+"F2.imprint","INTERSECT",VERTEX,{"derivedFrom":[subQ0,sQuery(id+"F2.wireOp",EDGE,"E13.11.2")]}),-1.0]])],"derivedFrom":subQ0})])],"isStart":true});}
            var Q107;
            Q107=makeQuery(id+"F3.opExtrude","CAP_EDGE",EDGE,{"disambiguationData":[OSD([sQuery(id+"F2.wireOp",EDGE,"E13.11.2")])],"isStart":true});
            var Q108;
            Q108=makeQuery(id+"F3.opExtrude","CAP_EDGE",EDGE,{"disambiguationData":[OSD([sQuery(id+"F2.wireOp",EDGE,"E13.11.0")])],"isStart":true});
            var Q109;
            {var subQ0=sQuery(id+"F2.wireOp",EDGE,"E0");Q109=makeQuery(id+"F3.opExtrude","CAP_EDGE",EDGE,{"disambiguationData":[OSD([subQ0]),TDD([makeQuery(id+"F2.imprint","IMPRINT",EDGE,{"disambiguationData":[TD([[makeQuery(id+"F2.imprint","INTERSECT",VERTEX,{"derivedFrom":[subQ0,sQuery(id+"F2.wireOp",EDGE,"E13.10.2")]}),-1.0]])],"derivedFrom":subQ0})])],"isStart":true});}
            var Q110;
            Q110=makeQuery(id+"F3.opExtrude","CAP_EDGE",EDGE,{"disambiguationData":[OSD([sQuery(id+"F2.wireOp",EDGE,"E13.10.2")])],"isStart":true});
            var Q111;
            Q111=makeQuery(id+"F3.opExtrude","CAP_EDGE",EDGE,{"disambiguationData":[OSD([sQuery(id+"F2.wireOp",EDGE,"E13.10.0")])],"isStart":true});
            var Q112;
            {var subQ0=sQuery(id+"F2.wireOp",EDGE,"E0");Q112=makeQuery(id+"F3.opExtrude","CAP_EDGE",EDGE,{"disambiguationData":[OSD([subQ0]),TDD([makeQuery(id+"F2.imprint","IMPRINT",EDGE,{"disambiguationData":[TD([[makeQuery(id+"F2.imprint","INTERSECT",VERTEX,{"derivedFrom":[subQ0,sQuery(id+"F2.wireOp",EDGE,"E13.9.2")]}),-1.0]])],"derivedFrom":subQ0})])],"isStart":true});}
            var Q113;
            Q113=makeQuery(id+"F3.opExtrude","CAP_EDGE",EDGE,{"disambiguationData":[OSD([sQuery(id+"F2.wireOp",EDGE,"E13.9.2")])],"isStart":true});
            var Q114;
            Q114=makeQuery(id+"F3.opExtrude","CAP_EDGE",EDGE,{"disambiguationData":[OSD([sQuery(id+"F2.wireOp",EDGE,"E13.9.0")])],"isStart":true});
            var Q115;
            {var subQ0=sQuery(id+"F2.wireOp",EDGE,"E0");Q115=makeQuery(id+"F3.opExtrude","CAP_EDGE",EDGE,{"disambiguationData":[OSD([subQ0]),TDD([makeQuery(id+"F2.imprint","IMPRINT",EDGE,{"disambiguationData":[TD([[makeQuery(id+"F2.imprint","INTERSECT",VERTEX,{"derivedFrom":[subQ0,sQuery(id+"F2.wireOp",EDGE,"E13.8.2")]}),-1.0]])],"derivedFrom":subQ0})])],"isStart":true});}
            var Q116;
            Q116=makeQuery(id+"F3.opExtrude","CAP_EDGE",EDGE,{"disambiguationData":[OSD([sQuery(id+"F2.wireOp",EDGE,"E13.8.2")])],"isStart":true});
            fillet(context, id + "F4", {"entities" : qUnion([Q0, Q1, Q2, Q3, Q4, Q5, Q6, Q7, Q8, Q9, Q10, Q11, Q12, Q13, Q14, Q15, Q16, Q17, Q18, Q19, Q20, Q21, Q22, Q23, Q24, Q25, Q26, Q27, Q28, Q29, Q30, Q31, Q32, Q33, Q34, Q35, Q36, Q37, Q38, Q39, Q40, Q41, Q42, Q43, Q44, Q45, Q46, Q47, Q48, Q49, Q50, Q51, Q52, Q53, Q54, Q55, Q56, Q57, Q58, Q59, Q60, Q61, Q62, Q63, Q64, Q65, Q66, Q67, Q68, Q69, Q70, Q71, Q72, Q73, Q74, Q75, Q76, Q77, Q78, Q79, Q80, Q81, Q82, Q83, Q84, Q85, Q86, Q87, Q88, Q89, Q90, Q91, Q92, Q93, Q94, Q95, Q96, Q97, Q98, Q99, Q100, Q101, Q102, Q103, Q104, Q105, Q106, Q107, Q108, Q109, Q110, Q111, Q112, Q113, Q114, Q115, Q116]), "radius" : (getVariable(context, 'TeethFillet')) * mm, "tangentPropagation" : true, "allowEdgeOverflow" : false});
        }
    });
